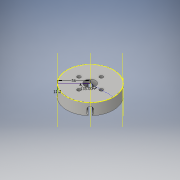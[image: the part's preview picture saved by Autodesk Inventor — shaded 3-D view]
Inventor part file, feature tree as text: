
AUTODESK INVENTOR PART (.ipt)
format: ipt  version: 2016 (Build 200138000, 138)  size: 270,848 bytes
history: native  units: in
note: dims shown in document units (in); Inventor stores cm internally (conversion verified against a paired STEP export)
features: sketch x10, extrude x4, plane x3, pattern_circular x3
ambient origin geometry x8: Origin, YZ Plane, XZ Plane, XY Plane, X Axis, Y Axis, Z Axis, Center Point
bodies: Solid1 (feature_tree)
feature tree (20):
  extrude  "Extrusion1"  Depth=2.1378in
  sketch  "Sketch2"  dims[d12=0.4921in d13=1.5748in d15=360.0deg]
  sketch  "Sketch3"  dims[d17=0.2992in d18=0.0in d21=2.2047in]
  extrude  "Extrusion2"  Depth=1.5748in TaperAngle=360.0deg
  sketch  "Sketch5"  dims[d36=1.5748in d37=360.0deg d39=0.5in]
  sketch  "Sketch6"  dims[d40=0.4409in]
  plane  "Work Plane9"
  plane  "Work Plane10"
  sketch  "Sketch11"  dims[d41=2.2047in]
  sketch  "Sketch12"  dims[d64=0.3504in]
  extrude  "Extrusion4"  Depth=2.2047in
  pattern_circular  "Circular Pattern2"  Count=10  [1 undecoded]
  plane  "Work Plane11"
  sketch  "Sketch13"  dims[d65=0.2126in]
  sketch  "Sketch14"  dims[d66=0.3504in d67=2.2047in d68=0.1181in d69=0.0in d70=0.0in d71=1.5748in d72=360.0deg d74=1.5748in d75=360.0deg d25=0.0394in d26=0.0394in]
  extrude  "Extrusion5"  Depth=0.5in
  pattern_circular  "Circular Pattern3"  [2 undecoded]
  pattern_circular  "Circular Pattern4"  Count=4 Angle=360.0deg
  sketch  "Sketch1"  dims[d8=1.1024in d9=0.0in d11=2.1378in]
  sketch  "Sketch4"  dims[d22=135.0deg d32=3.937in d33=1.9685in d34=0.0in d35=0.0in]
note: 3 required parameter values undecoded (feature->parameter linkage not recoverable at this tier; creation-order binding heuristic only, values carry confidence <= 0.55)
